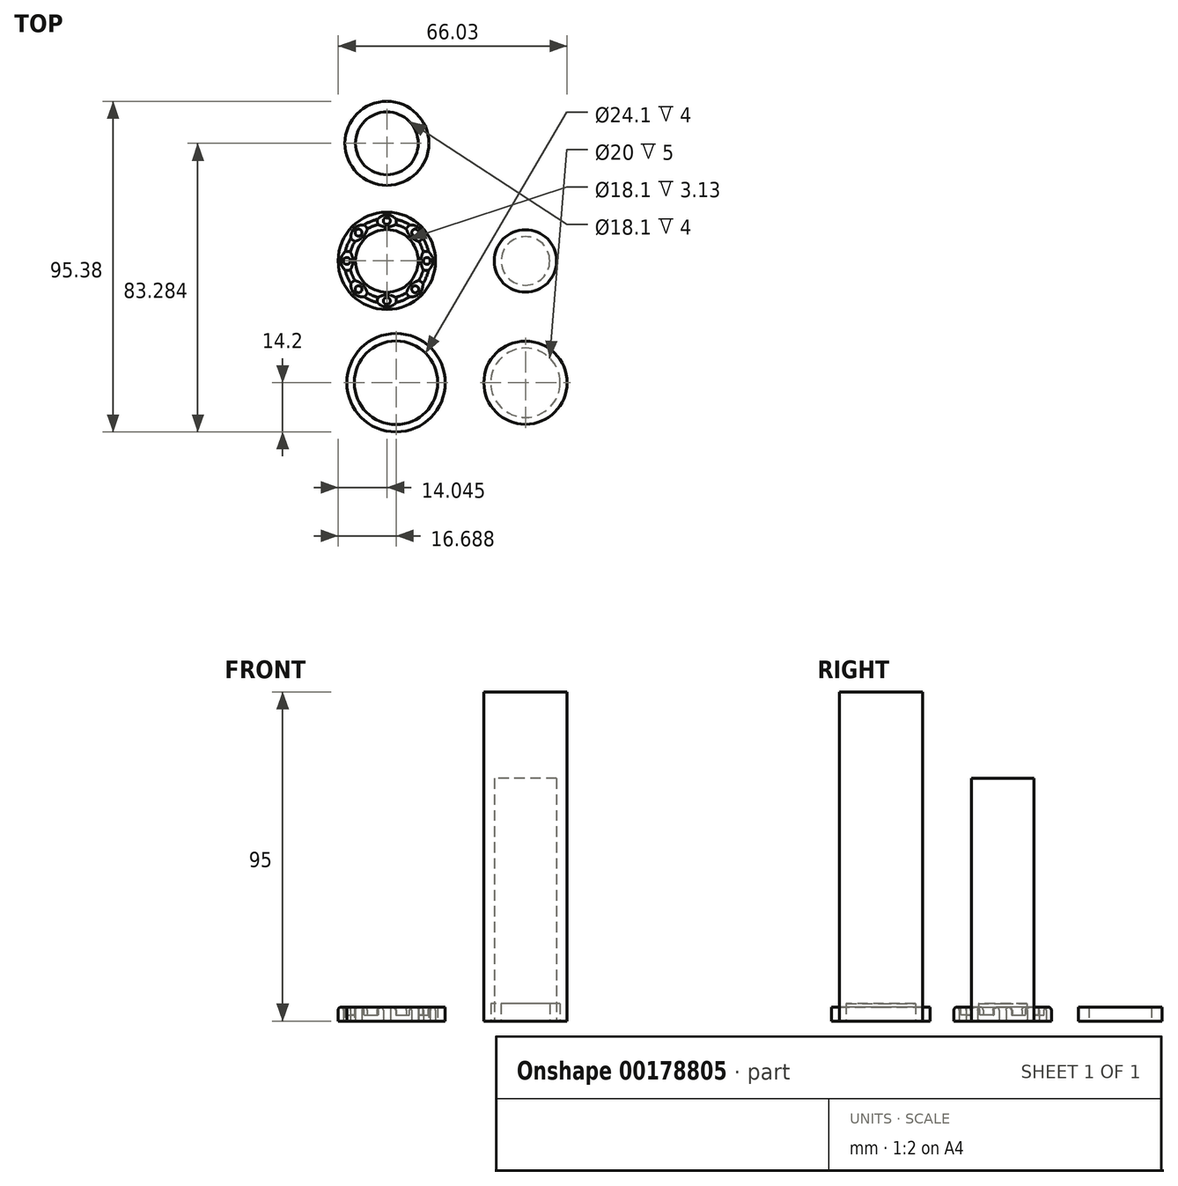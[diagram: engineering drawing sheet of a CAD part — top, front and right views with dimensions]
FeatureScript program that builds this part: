
annotation { "Feature Type Name" : "Feature", "Feature Type Description" : "" }
export const myFeature = defineFeature(function(context is Context, id is Id, definition is map)
    precondition{}
    {
        {
            var Q0;
            Q0=qCreatedBy(makeId("Top.planeOp"),FACE);
            var sketch = newSketch(context, id + "F0", { "sketchPlane" : qUnion([Q0])});
            skCircle(sketch, "E0", {"center": v(0, 0) * mm, "radius": 12 * mm});
            skCircle(sketch, "E1", {"center": v(0, 35.15) * mm, "radius": 9 * mm});
            skCircle(sketch, "E2", {"center": v(-39.98, 35.15) * mm, "radius": 9.05 * mm});
            skCircle(sketch, "E3", {"center": v(-39.98, 35.15) * mm, "radius": 14.05 * mm});
            skCircle(sketch, "E4", {"center": v(-37.34, 0) * mm, "radius": 12.05 * mm});
            skCircle(sketch, "E5", {"center": v(-37.34, 0) * mm, "radius": 14.2 * mm});
            skCircle(sketch, "E6", {"center": v(-39.98, 69.08) * mm, "radius": 9.05 * mm});
            skCircle(sketch, "E7", {"center": v(-39.98, 69.08) * mm, "radius": 12.1 * mm});
            skCircle(sketch, "E8", {"center": v(0, 35.15) * mm, "radius": 7 * mm});
            skCircle(sketch, "E9", {"center": v(0, 0) * mm, "radius": 10 * mm});
            skCircle(sketch, "E10", {"center": v(-51.53, 35.15) * mm, "radius": 1 * mm});
            skCircle(sketch, "E11.1.0", {"center": v(-48.15, 26.98) * mm, "radius": 1 * mm});
            skCircle(sketch, "E11.2.0", {"center": v(-39.98, 23.6) * mm, "radius": 1 * mm});
            skCircle(sketch, "E11.3.0", {"center": v(-31.82, 26.98) * mm, "radius": 1 * mm});
            skCircle(sketch, "E11.4.0", {"center": v(-28.43, 35.15) * mm, "radius": 1 * mm});
            skCircle(sketch, "E11.5.0", {"center": v(-31.82, 43.32) * mm, "radius": 1 * mm});
            skCircle(sketch, "E11.6.0", {"center": v(-39.98, 46.7) * mm, "radius": 1 * mm});
            skCircle(sketch, "E11.7.0", {"center": v(-48.15, 43.32) * mm, "radius": 1 * mm});
            skSolve(sketch);
        }
        {
            var Q0;
            Q0=makeQuery(id+"F0.imprint","IMPRINT",FACE,{"disambiguationData":[TD([[makeQuery(id+"F0.imprint","IMPRINT",EDGE,{"derivedFrom":sQuery(id+"F0.wireOp",EDGE,"E2")}),-1.0]])]});
            var Q1;
            Q1=makeQuery(id+"F0.imprint","IMPRINT",FACE,{"disambiguationData":[TD([[makeQuery(id+"F0.imprint","IMPRINT",EDGE,{"derivedFrom":sQuery(id+"F0.wireOp",EDGE,"E4")}),-1.0]])]});
            var Q2;
            Q2=makeQuery(id+"F0.imprint","IMPRINT",FACE,{"disambiguationData":[TD([[makeQuery(id+"F0.imprint","IMPRINT",EDGE,{"derivedFrom":sQuery(id+"F0.wireOp",EDGE,"E6")}),-1.0]])]});
            extrude(context, id + "F1", {"entities" : qUnion([Q0, Q1, Q2]), "depth" : 4 * mm});
        }
        {
            var Q0;
            Q0=makeQuery(id+"F0.imprint","IMPRINT",FACE,{"disambiguationData":[TD([[makeQuery(id+"F0.imprint","IMPRINT",EDGE,{"derivedFrom":sQuery(id+"F0.wireOp",EDGE,"E1")}),1.0]])]});
            var Q1;
            Q1=makeQuery(id+"F0.imprint","IMPRINT",FACE,{"disambiguationData":[TD([[makeQuery(id+"F0.imprint","IMPRINT",EDGE,{"derivedFrom":sQuery(id+"F0.wireOp",EDGE,"E8")}),1.0]])]});
            extrude(context, id + "F2", {"entities" : qUnion([Q0, Q1]), "depth" : 70 * mm});
        }
        {
            var Q0;
            Q0=makeQuery(id+"F0.imprint","IMPRINT",FACE,{"disambiguationData":[TD([[makeQuery(id+"F0.imprint","IMPRINT",EDGE,{"derivedFrom":sQuery(id+"F0.wireOp",EDGE,"E0")}),1.0]])]});
            var Q1;
            Q1=makeQuery(id+"F0.imprint","IMPRINT",FACE,{"disambiguationData":[TD([[makeQuery(id+"F0.imprint","IMPRINT",EDGE,{"derivedFrom":sQuery(id+"F0.wireOp",EDGE,"E9")}),1.0]])]});
            extrude(context, id + "F3", {"entities" : qUnion([Q0, Q1]), "depth" : 95 * mm});
        }
        {
            var Q0;
            Q0=makeQuery(id+"F0.imprint","IMPRINT",FACE,{"disambiguationData":[TD([[makeQuery(id+"F0.imprint","IMPRINT",EDGE,{"derivedFrom":sQuery(id+"F0.wireOp",EDGE,"E8")}),1.0]])]});
            extrude(context, id + "F4", {"entities" : qUnion([Q0]), "operationType" : NewBodyOperationType.REMOVE, "depth" : 5 * mm});
        }
        {
            var Q0;
            Q0=makeQuery(id+"F0.imprint","IMPRINT",FACE,{"disambiguationData":[TD([[makeQuery(id+"F0.imprint","IMPRINT",EDGE,{"derivedFrom":sQuery(id+"F0.wireOp",EDGE,"E9")}),1.0]])]});
            var Q1;
            Q1=sQuery(id+"F0.wireOp",EDGE,"E9");
            extrude(context, id + "F5", {"entities" : qUnion([Q0]), "operationType" : NewBodyOperationType.REMOVE, "surfaceEntities" : qUnion([Q1]), "depth" : 5 * mm});
        }
        {
            var Q0;
            Q0=makeQuery(id+"F1.opExtrude","CAP_FACE",FACE,{"disambiguationData":[OSD([sQuery(id+"F0.wireOp",EDGE,"E2"),sQuery(id+"F0.wireOp",EDGE,"E3")])],"isStart":false});
            shell(context, id + "F6", {"entities" : qUnion([Q0]), "thickness" : 1.75 * mm});
        }
        {
            var Q0;
            Q0=makeQuery(id+"F1.opExtrude","CAP_FACE",FACE,{"disambiguationData":[OSD([sQuery(id+"F0.wireOp",EDGE,"E2"),sQuery(id+"F0.wireOp",EDGE,"E3"),sQuery(id+"F0.wireOp",EDGE,"E10"),sQuery(id+"F0.wireOp",EDGE,"E11.1.0"),sQuery(id+"F0.wireOp",EDGE,"E11.2.0"),sQuery(id+"F0.wireOp",EDGE,"E11.3.0"),sQuery(id+"F0.wireOp",EDGE,"E11.4.0"),sQuery(id+"F0.wireOp",EDGE,"E11.5.0"),sQuery(id+"F0.wireOp",EDGE,"E11.6.0"),sQuery(id+"F0.wireOp",EDGE,"E11.7.0")])],"isStart":false});
            fillet(context, id + "F7", {"entities" : qUnion([Q0]), "radius" : 0.87 * mm, "tangentPropagation" : true, "allowEdgeOverflow" : false});
        }
    });
